# Revit family: Symetra Plus_Straight_Final
name_source: partatom
category: Furniture
revit_build: Autodesk Revit Architecture 2012 (Build: 20110309_2315(x64)
units: mm (PartAtom-declared; Revit-internal decimal feet)

## types (1)
- Symetra Plus_Straight_Final
    27" Swingarm = Yes
    30" Swingarm = No
    Actual Depth = 1' - 9"
    Assembly Code = E2010
    Description = Lecture hall tables with seats
    Leg Finish = <By Category>
    Leg Set Back = 0' - 5 1/2"
    Manufacturer = Navetta
    Max Depth = 2' - 6"
    Min Depth = 1' - 6"
    Min. Table Length = 60in.
    Model = Symetra Plus
    Modest & End Panel Finish = <By Category>
    Modesty Panel 12"H = Yes
    Modesty Panel 14"H = Yes
    Modesty Panel 26"H = No
    Modesty Panel Actual Height = 1' - 0"
    Modesty Panel Laminate = Yes
    Modesty Panel Steel = No
    Power Finish = <By Category>
    Seat Type FLOU = No
    Seat Type Nortwood = No
    Seat Type Trilogy = No
    Seat Type Zero 7 = Yes
    Seat and Back Finish = <By Category>
    Standard Modesty Panel Heights = 12,14,26 in.
    Standard Table Depths = 18-30 in.
    Table Depth = 1' - 9"
    Table Height = 2' - 5"
    Table Top Finish = <By Category>
    URL = http://navettadesign.com
    Upholstery = <By Category>
    Version = 1

## geometry (parser evidence)
native form markers: Blend x2, Sweep x53
no freeform markers — native parametric forms only
